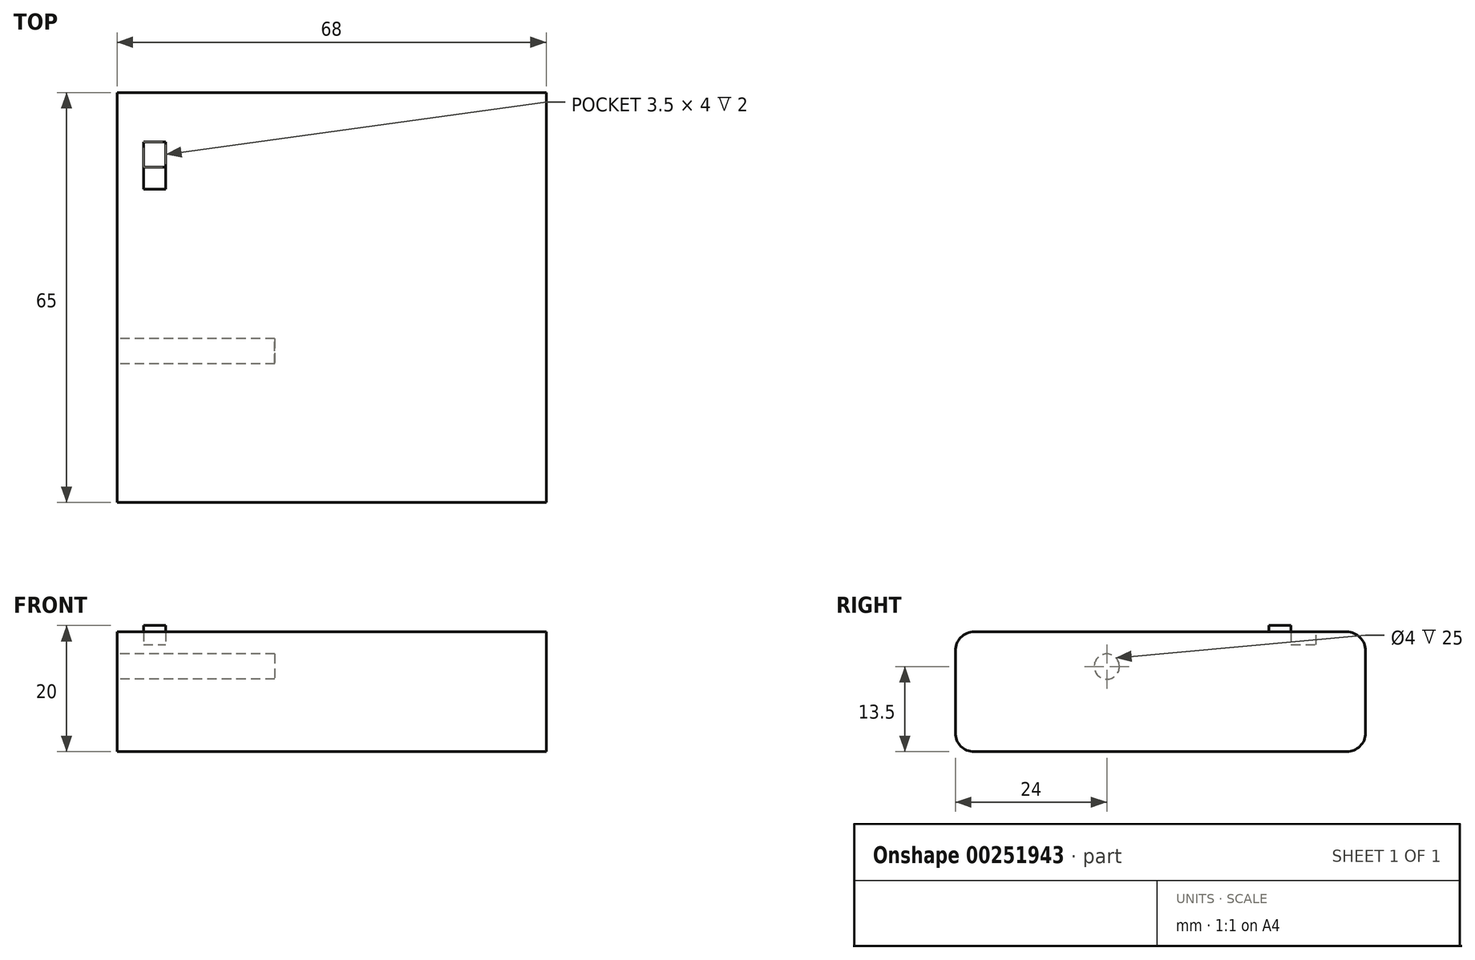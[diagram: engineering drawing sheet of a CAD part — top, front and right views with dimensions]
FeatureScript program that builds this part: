
annotation { "Feature Type Name" : "Feature", "Feature Type Description" : "" }
export const myFeature = defineFeature(function(context is Context, id is Id, definition is map)
    precondition{}
    {
        {
            var Q0;
            Q0=qCreatedBy(makeId("Right.planeOp"),FACE);
            var sketch = newSketch(context, id + "F0", { "sketchPlane" : qUnion([Q0])});
            skLineSegment(sketch, "E0.bottom", {"start": v(29.5, -9.5) * mm, "end": v(-29.5, -9.5) * mm});
            skLineSegment(sketch, "E0.top", {"start": v(29.5, 9.5) * mm, "end": v(-29.5, 9.5) * mm});
            skLineSegment(sketch, "E0.left", {"start": v(32.5, -6.5) * mm, "end": v(32.5, 6.5) * mm});
            skLineSegment(sketch, "E0.right", {"start": v(-32.5, -6.5) * mm, "end": v(-32.5, 6.5) * mm});
            skPoint(sketch, "E0.middle", {"position": v(0, 0) * mm});
            skPoint(sketch, "E1.visualSharp", {"position": v(-32.5, 9.5) * mm});
            skArc(sketch, "E1.filletArc", {"start": v(-29.5, 9.5) * mm, "mid": v(-31.62, 8.62) * mm, "end": v(-32.5, 6.5) * mm});
            skPoint(sketch, "E2.visualSharp", {"position": v(32.5, 9.5) * mm});
            skArc(sketch, "E2.filletArc", {"start": v(32.5, 6.5) * mm, "mid": v(31.62, 8.62) * mm, "end": v(29.5, 9.5) * mm});
            skPoint(sketch, "E3.visualSharp", {"position": v(32.5, -9.5) * mm});
            skArc(sketch, "E3.filletArc", {"start": v(29.5, -9.5) * mm, "mid": v(31.62, -8.62) * mm, "end": v(32.5, -6.5) * mm});
            skPoint(sketch, "E4.visualSharp", {"position": v(-32.5, -9.5) * mm});
            skArc(sketch, "E4.filletArc", {"start": v(-32.5, -6.5) * mm, "mid": v(-31.62, -8.62) * mm, "end": v(-29.5, -9.5) * mm});
            skSolve(sketch);
        }
        {
            var Q0;
            Q0=makeQuery(id+"F0.imprint","IMPRINT",FACE,{"disambiguationData":[TD([[makeQuery(id+"F0.imprint","IMPRINT",EDGE,{"derivedFrom":sQuery(id+"F0.wireOp",EDGE,"E0.bottom")}),-1.0]])]});
            extrude(context, id + "F1", {"entities" : qUnion([Q0]), "depth" : 68 * mm});
        }
        {
            var Q0;
            Q0=makeQuery(id+"F1.opExtrude","SWEPT_FACE",FACE,{"disambiguationData":[OSD([sQuery(id+"F0.wireOp",EDGE,"E0.top")])]});
            var sketch = newSketch(context, id + "F2", { "sketchPlane" : qUnion([Q0])});
            skLineSegment(sketch, "E5.bottom", {"start": v(4.2, 17.2) * mm, "end": v(7.7, 17.2) * mm});
            skLineSegment(sketch, "E5.top", {"start": v(4.2, 24.7) * mm, "end": v(7.7, 24.7) * mm});
            skLineSegment(sketch, "E5.left", {"start": v(4.2, 17.2) * mm, "end": v(4.2, 24.7) * mm});
            skLineSegment(sketch, "E5.right", {"start": v(7.7, 17.2) * mm, "end": v(7.7, 24.7) * mm});
            skSolve(sketch);
        }
        {
            var Q0;
            Q0=makeQuery(id+"F2.imprint","IMPRINT",FACE,{"disambiguationData":[TD([[makeQuery(id+"F2.imprint","IMPRINT",EDGE,{"derivedFrom":sQuery(id+"F2.wireOp",EDGE,"E5.bottom")}),1.0]])]});
            extrude(context, id + "F3", {"entities" : qUnion([Q0]), "operationType" : NewBodyOperationType.REMOVE, "oppositeDirection" : true, "depth" : 2 * mm});
        }
        {
            var Q0;
            Q0=makeQuery(id+"F1.opExtrude","CAP_FACE",FACE,{"disambiguationData":[OSD([sQuery(id+"F0.wireOp",EDGE,"E0.bottom"),sQuery(id+"F0.wireOp",EDGE,"E0.top"),sQuery(id+"F0.wireOp",EDGE,"E0.left"),sQuery(id+"F0.wireOp",EDGE,"E0.right"),sQuery(id+"F0.wireOp",EDGE,"E1.filletArc"),sQuery(id+"F0.wireOp",EDGE,"E2.filletArc"),sQuery(id+"F0.wireOp",EDGE,"E3.filletArc"),sQuery(id+"F0.wireOp",EDGE,"E4.filletArc")])],"isStart":true});
            var sketch = newSketch(context, id + "F4", { "sketchPlane" : qUnion([Q0])});
            skCircle(sketch, "E6", {"center": v(8.5, 4) * mm, "radius": 2 * mm});
            skSolve(sketch);
        }
        {
            var Q0;
            Q0=makeQuery(id+"F4.imprint","IMPRINT",FACE,{"disambiguationData":[TD([[makeQuery(id+"F4.imprint","IMPRINT",EDGE,{"derivedFrom":sQuery(id+"F4.wireOp",EDGE,"E6")}),1.0]])]});
            extrude(context, id + "F5", {"entities" : qUnion([Q0]), "operationType" : NewBodyOperationType.REMOVE, "oppositeDirection" : true, "depth" : 25 * mm});
        }
        {
            var Q0;
            Q0=makeQuery(id+"F3.boolean.opBoolean","COPY",FACE,{"derivedFrom":makeQuery(id+"F3.opExtrude","CAP_FACE",FACE,{"disambiguationData":[OSD([sQuery(id+"F2.wireOp",EDGE,"E5.bottom"),sQuery(id+"F2.wireOp",EDGE,"E5.top"),sQuery(id+"F2.wireOp",EDGE,"E5.left"),sQuery(id+"F2.wireOp",EDGE,"E5.right")])],"isStart":false})});
            var sketch = newSketch(context, id + "F6", { "sketchPlane" : qUnion([Q0])});
            skLineSegment(sketch, "E7.bottom", {"start": v(4.2, 17.2) * mm, "end": v(7.7, 17.2) * mm});
            skLineSegment(sketch, "E7.top", {"start": v(4.2, 20.7) * mm, "end": v(7.7, 20.7) * mm});
            skLineSegment(sketch, "E7.left", {"start": v(4.2, 17.2) * mm, "end": v(4.2, 20.7) * mm});
            skLineSegment(sketch, "E7.right", {"start": v(7.7, 17.2) * mm, "end": v(7.7, 20.7) * mm});
            skSolve(sketch);
        }
        {
            var Q0;
            Q0=makeQuery(id+"F6.imprint","IMPRINT",FACE,{"disambiguationData":[TD([[makeQuery(id+"F6.imprint","IMPRINT",EDGE,{"derivedFrom":sQuery(id+"F6.wireOp",EDGE,"E7.bottom")}),1.0]])]});
            extrude(context, id + "F7", {"entities" : qUnion([Q0]), "operationType" : NewBodyOperationType.ADD, "depth" : 3 * mm});
        }
    });
